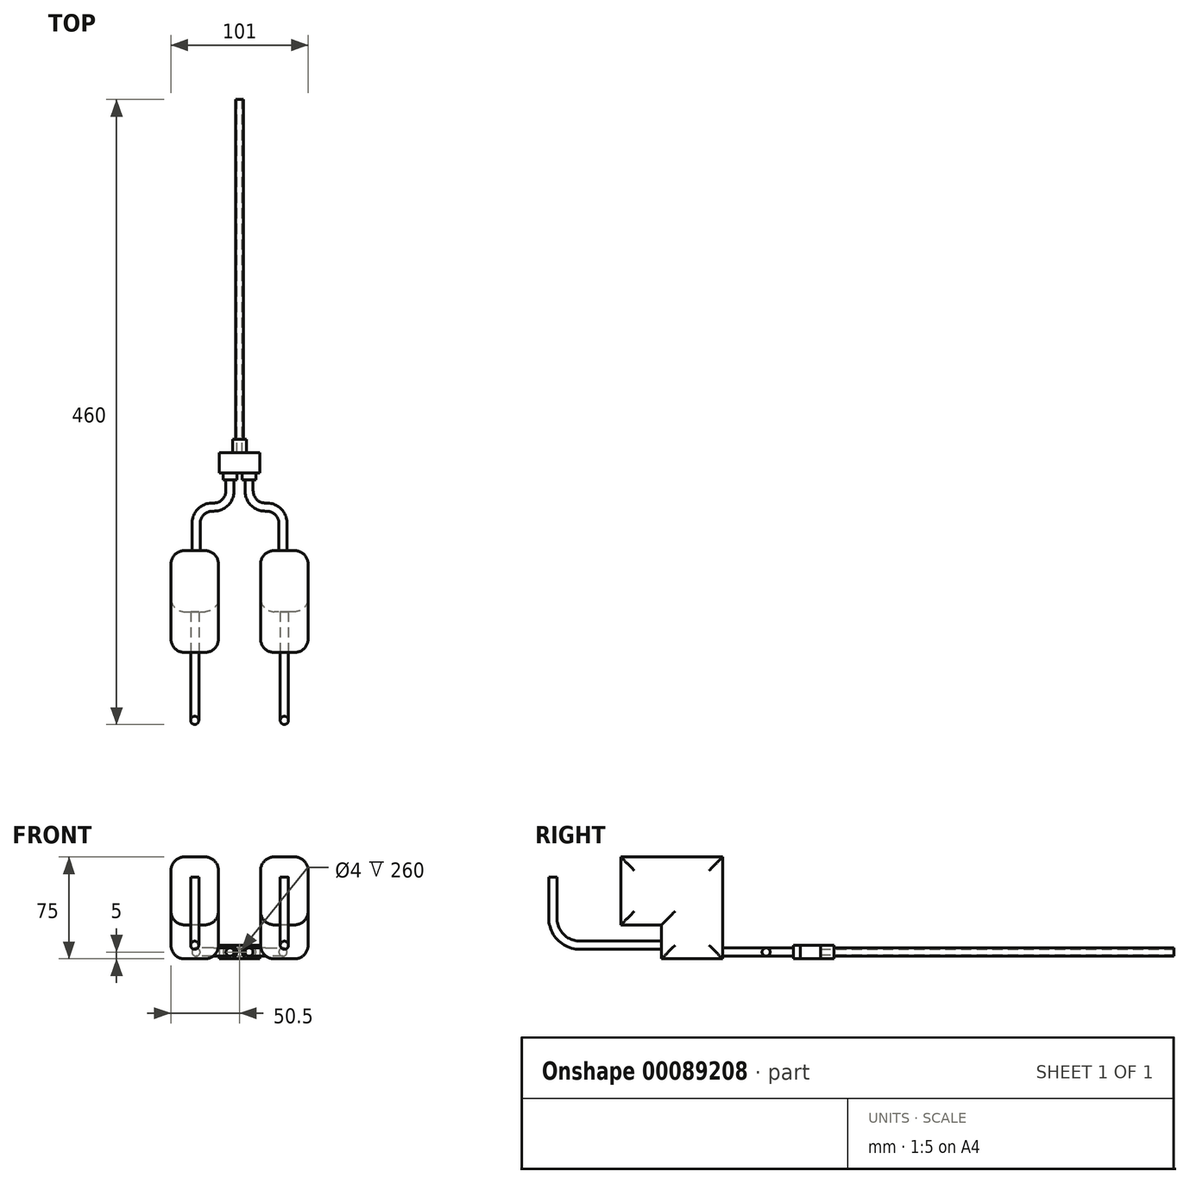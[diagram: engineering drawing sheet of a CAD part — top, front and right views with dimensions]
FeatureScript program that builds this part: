
annotation { "Feature Type Name" : "Feature", "Feature Type Description" : "" }
export const myFeature = defineFeature(function(context is Context, id is Id, definition is map)
    precondition{}
    {
        {
            var Q0;
            Q0=qCreatedBy(makeId("Front.planeOp"),FACE);
            var sketch = newSketch(context, id + "F0", { "sketchPlane" : qUnion([Q0])});
            skCircle(sketch, "E0", {"center": v(0, 0) * mm, "radius": 3 * mm});
            skCircle(sketch, "E1", {"center": v(0, 0) * mm, "radius": 2 * mm});
            skSolve(sketch);
        }
        {
            var Q0;
            Q0=makeQuery(id+"F0.imprint","IMPRINT",FACE,{"disambiguationData":[TD([[makeQuery(id+"F0.imprint","IMPRINT",EDGE,{"derivedFrom":sQuery(id+"F0.wireOp",EDGE,"E0")}),1.0]])]});
            extrude(context, id + "F1", {"entities" : qUnion([Q0]), "depth" : 250 * mm});
        }
        {
            var Q0;
            Q0=makeQuery(id+"F1.opExtrude","CAP_FACE",FACE,{"disambiguationData":[OSD([sQuery(id+"F0.wireOp",EDGE,"E0"),sQuery(id+"F0.wireOp",EDGE,"E1")])],"isStart":false});
            var sketch = newSketch(context, id + "F2", { "sketchPlane" : qUnion([Q0])});
            skCircle(sketch, "E2", {"center": v(0, 0) * mm, "radius": 5 * mm});
            skSolve(sketch);
        }
        {
            var Q0;
            Q0=makeQuery(id+"F2.imprint","IMPRINT",FACE,{"disambiguationData":[TD([[makeQuery(id+"F2.imprint","IMPRINT",EDGE,{"derivedFrom":sQuery(id+"F2.wireOp",EDGE,"E2")}),1.0]])]});
            var Q1;
            Q1=makeQuery(id+"F2.imprint","IMPRINT",FACE,{"disambiguationData":[TD([[makeQuery(id+"F2.imprint","IMPRINT",EDGE,{"derivedFrom":makeQuery(id+"F1.opExtrude","CAP_EDGE",EDGE,{"disambiguationData":[OSD([sQuery(id+"F0.wireOp",EDGE,"E0")])],"isStart":false})}),1.0]])]});
            extrude(context, id + "F3", {"entities" : qUnion([Q0, Q1]), "operationType" : NewBodyOperationType.ADD, "depth" : 10 * mm});
        }
        {
            var Q0;
            Q0=makeQuery(id+"F3.opExtrude","CAP_FACE",FACE,{"disambiguationData":[OSD([sQuery(id+"F0.wireOp",EDGE,"E1"),sQuery(id+"F2.wireOp",EDGE,"E2")])],"isStart":false});
            var sketch = newSketch(context, id + "F4", { "sketchPlane" : qUnion([Q0])});
            skLineSegment(sketch, "E3.bottom", {"start": v(15, 5) * mm, "end": v(-15, 5) * mm});
            skLineSegment(sketch, "E3.top", {"start": v(15, -5) * mm, "end": v(-15, -5) * mm});
            skLineSegment(sketch, "E3.left", {"start": v(15, 5) * mm, "end": v(15, -5) * mm});
            skLineSegment(sketch, "E3.right", {"start": v(-15, 5) * mm, "end": v(-15, -5) * mm});
            skSolve(sketch);
        }
        {
            var Q0;
            {var subQ0=sQuery(id+"F4.wireOp",EDGE,"E3.right");Q0=makeQuery(id+"F4.imprint","IMPRINT",FACE,{"disambiguationData":[TD([[makeQuery(id+"F4.imprint","IMPRINT",EDGE,{"derivedFrom":subQ0}),1.0]])]});}
            var Q1;
            Q1=makeQuery(id+"F4.imprint","IMPRINT",FACE,{"disambiguationData":[TD([[makeQuery(id+"F4.imprint","IMPRINT",EDGE,{"derivedFrom":makeQuery(id+"F3.opExtrude","CAP_EDGE",EDGE,{"disambiguationData":[OSD([sQuery(id+"F0.wireOp",EDGE,"E1")])],"isStart":false})}),-1.0]])]});
            var Q2;
            {var subQ0=sQuery(id+"F4.wireOp",EDGE,"E3.left");Q2=makeQuery(id+"F4.imprint","IMPRINT",FACE,{"disambiguationData":[TD([[makeQuery(id+"F4.imprint","IMPRINT",EDGE,{"derivedFrom":subQ0}),-1.0]])]});}
            var Q3;
            Q3=makeQuery(id+"F4.imprint","IMPRINT",FACE,{"disambiguationData":[TD([[makeQuery(id+"F4.imprint","IMPRINT",EDGE,{"derivedFrom":makeQuery(id+"F3.opExtrude","CAP_EDGE",EDGE,{"disambiguationData":[OSD([sQuery(id+"F0.wireOp",EDGE,"E1")])],"isStart":false})}),1.0]])]});
            extrude(context, id + "F5", {"entities" : qUnion([Q0, Q1, Q2, Q3]), "operationType" : NewBodyOperationType.ADD, "depth" : 15 * mm});
        }
        {
            var Q0;
            Q0=makeQuery(id+"F5.opExtrude","CAP_FACE",FACE,{"disambiguationData":[OSD([sQuery(id+"F4.wireOp",EDGE,"E3.bottom"),sQuery(id+"F4.wireOp",EDGE,"E3.top"),sQuery(id+"F4.wireOp",EDGE,"E3.left"),sQuery(id+"F4.wireOp",EDGE,"E3.right")])],"isStart":false});
            var sketch = newSketch(context, id + "F6", { "sketchPlane" : qUnion([Q0])});
            skCircle(sketch, "E4", {"center": v(-7, 0) * mm, "radius": 5 * mm});
            skCircle(sketch, "E5", {"center": v(7, 0) * mm, "radius": 5 * mm});
            skCircle(sketch, "E6", {"center": v(7, 0) * mm, "radius": 3 * mm});
            skCircle(sketch, "E7", {"center": v(-7, 0) * mm, "radius": 3 * mm});
            skSolve(sketch);
        }
        {
            var Q0;
            Q0=makeQuery(id+"F6.imprint","IMPRINT",FACE,{"disambiguationData":[TD([[makeQuery(id+"F6.imprint","IMPRINT",EDGE,{"derivedFrom":sQuery(id+"F6.wireOp",EDGE,"E7")}),-1.0]])]});
            var Q1;
            Q1=makeQuery(id+"F6.imprint","IMPRINT",FACE,{"disambiguationData":[TD([[makeQuery(id+"F6.imprint","IMPRINT",EDGE,{"derivedFrom":sQuery(id+"F6.wireOp",EDGE,"E6")}),-1.0]])]});
            extrude(context, id + "F7", {"entities" : qUnion([Q0, Q1]), "operationType" : NewBodyOperationType.ADD, "depth" : 5 * mm});
        }
        {
            var Q0;
            Q0=makeQuery(id+"F7.boolean.opBoolean","SPLIT",FACE,{"disambiguationData":[TD([makeQuery(id+"F7.opExtrude","SWEPT_FACE",FACE,{"disambiguationData":[OSD([sQuery(id+"F6.wireOp",EDGE,"E7")])]})])],"derivedFrom":makeQuery(id+"F5.opExtrude","CAP_FACE",FACE,{"disambiguationData":[OSD([sQuery(id+"F4.wireOp",EDGE,"E3.bottom"),sQuery(id+"F4.wireOp",EDGE,"E3.top"),sQuery(id+"F4.wireOp",EDGE,"E3.left"),sQuery(id+"F4.wireOp",EDGE,"E3.right")])],"isStart":false})});
            var sketch = newSketch(context, id + "F8", { "sketchPlane" : qUnion([Q0])});
            skCircle(sketch, "E8", {"center": v(-7, 0) * mm, "radius": 3 * mm});
            skCircle(sketch, "E9", {"center": v(7, 0) * mm, "radius": 3 * mm});
            skSolve(sketch);
        }
        {
            var Q0;
            Q0=qCreatedBy(makeId("Top.planeOp"),FACE);
            var sketch = newSketch(context, id + "F9", { "sketchPlane" : qUnion([Q0])});
            skLineSegment(sketch, "E10", {"start": v(-7, -275) * mm, "end": v(-7, -288) * mm});
            skLineSegment(sketch, "E11", {"start": v(-19, -300) * mm, "end": v(-20, -300) * mm});
            skLineSegment(sketch, "E12", {"start": v(7, -275) * mm, "end": v(7, -288) * mm});
            skLineSegment(sketch, "E13", {"start": v(19, -300) * mm, "end": v(20, -300) * mm});
            skLineSegment(sketch, "E14", {"start": v(-32, -312) * mm, "end": v(-32, -332) * mm});
            skLineSegment(sketch, "E15", {"start": v(32, -312) * mm, "end": v(32, -332) * mm});
            skPoint(sketch, "E16.visualSharp", {"position": v(-32, -300) * mm});
            skArc(sketch, "E16.filletArc", {"start": v(-20, -300) * mm, "mid": v(-28.49, -303.51) * mm, "end": v(-32, -312) * mm});
            skPoint(sketch, "E17.visualSharp", {"position": v(-7, -300) * mm});
            skArc(sketch, "E17.filletArc", {"start": v(-19, -300) * mm, "mid": v(-10.51, -296.49) * mm, "end": v(-7, -288) * mm});
            skPoint(sketch, "E18.visualSharp", {"position": v(32, -300) * mm});
            skArc(sketch, "E18.filletArc", {"start": v(32, -312) * mm, "mid": v(28.49, -303.51) * mm, "end": v(20, -300) * mm});
            skPoint(sketch, "E19.visualSharp", {"position": v(7, -300) * mm});
            skArc(sketch, "E19.filletArc", {"start": v(7, -288) * mm, "mid": v(10.51, -296.49) * mm, "end": v(19, -300) * mm});
            skSolve(sketch);
        }
        {
            var Q0;
            Q0=makeQuery(id+"F8.imprint","IMPRINT",FACE,{"disambiguationData":[TD([[makeQuery(id+"F8.imprint","IMPRINT",EDGE,{"derivedFrom":sQuery(id+"F8.wireOp",EDGE,"E8")}),1.0]])]});
            var Q1;
            Q1=sQuery(id+"F9.wireOp",EDGE,"E10");
            var Q2;
            Q2=sQuery(id+"F9.wireOp",EDGE,"E17.filletArc");
            var Q3;
            Q3=sQuery(id+"F9.wireOp",EDGE,"E11");
            var Q4;
            Q4=sQuery(id+"F9.wireOp",EDGE,"E16.filletArc");
            var Q5;
            Q5=sQuery(id+"F9.wireOp",EDGE,"E14");
            sweep(context, id + "F10", {"operationType" : NewBodyOperationType.ADD, "profiles" : qUnion([Q0]), "path" : qUnion([Q1, Q2, Q3, Q4, Q5])});
        }
        {
            var Q0;
            Q0=makeQuery(id+"F1.opExtrude","SWEPT_BODY",BODY,{"disambiguationData":[OSD([sQuery(id+"F0.wireOp",EDGE,"E0"),sQuery(id+"F0.wireOp",EDGE,"E1")])]});
            var Q1;
            Q1=qCreatedBy(makeId("Right.planeOp"),FACE);
            mirror(context, id + "F11", {"operationType" : NewBodyOperationType.ADD, "entities" : qUnion([Q0]), "mirrorPlane" : qUnion([Q1])});
        }
        {
            var Q0;
            Q0=makeQuery(id+"F10.opSweep","CAP_FACE",FACE,{"disambiguationData":[OSD([sQuery(id+"F8.wireOp",EDGE,"E8"),sQuery(id+"F9.wireOp",VERTEX,"E14.end")])],"isStart":false});
            var sketch = newSketch(context, id + "F12", { "sketchPlane" : qUnion([Q0])});
            skLineSegment(sketch, "E20.bottom", {"start": v(-50.5, -5) * mm, "end": v(-15.5, -5) * mm});
            skLineSegment(sketch, "E20.top", {"start": v(-50.5, 70) * mm, "end": v(-15.5, 70) * mm});
            skLineSegment(sketch, "E20.left", {"start": v(-50.5, -5) * mm, "end": v(-50.5, 70) * mm});
            skLineSegment(sketch, "E20.right", {"start": v(-15.5, -5) * mm, "end": v(-15.5, 70) * mm});
            skLineSegment(sketch, "E21.bottom", {"start": v(15.5, -5) * mm, "end": v(50.5, -5) * mm});
            skLineSegment(sketch, "E21.top", {"start": v(15.5, 70) * mm, "end": v(50.5, 70) * mm});
            skLineSegment(sketch, "E21.left", {"start": v(15.5, -5) * mm, "end": v(15.5, 70) * mm});
            skLineSegment(sketch, "E21.right", {"start": v(50.5, -5) * mm, "end": v(50.5, 70) * mm});
            skSolve(sketch);
        }
        {
            var Q0;
            Q0=makeQuery(id+"F12.imprint","IMPRINT",FACE,{"disambiguationData":[TD([[makeQuery(id+"F12.imprint","IMPRINT",EDGE,{"derivedFrom":sQuery(id+"F12.wireOp",EDGE,"E20.bottom")}),1.0]])]});
            var Q1;
            Q1=makeQuery(id+"F12.imprint","IMPRINT",FACE,{"disambiguationData":[TD([[makeQuery(id+"F12.imprint","IMPRINT",EDGE,{"derivedFrom":sQuery(id+"F12.wireOp",EDGE,"E21.bottom")}),1.0]])]});
            var Q2;
            Q2=makeQuery(id+"F12.imprint","IMPRINT",FACE,{"disambiguationData":[TD([[makeQuery(id+"F12.imprint","IMPRINT",EDGE,{"derivedFrom":makeQuery(id+"F10.opSweep","CAP_EDGE",EDGE,{"disambiguationData":[OSD([sQuery(id+"F8.wireOp",EDGE,"E8"),sQuery(id+"F9.wireOp",VERTEX,"E14.end")])],"isStart":false})}),1.0]])]});
            extrude(context, id + "F13", {"entities" : qUnion([Q0, Q1, Q2]), "operationType" : NewBodyOperationType.ADD, "depth" : 75 * mm});
        }
        {
            var Q0;
            Q0=makeQuery(id+"F13.opExtrude","CAP_FACE",FACE,{"disambiguationData":[OSD([sQuery(id+"F12.wireOp",EDGE,"E20.bottom"),sQuery(id+"F12.wireOp",EDGE,"E20.top"),sQuery(id+"F12.wireOp",EDGE,"E20.left"),sQuery(id+"F12.wireOp",EDGE,"E20.right")])],"isStart":false});
            var sketch = newSketch(context, id + "F14", { "sketchPlane" : qUnion([Q0])});
            skLineSegment(sketch, "E22.bottom", {"start": v(-15.5, -5) * mm, "end": v(-50.5, -5) * mm});
            skLineSegment(sketch, "E22.top", {"start": v(-15.5, 20) * mm, "end": v(-50.5, 20) * mm});
            skLineSegment(sketch, "E22.left", {"start": v(-15.5, -5) * mm, "end": v(-15.5, 20) * mm});
            skLineSegment(sketch, "E22.right", {"start": v(-50.5, -5) * mm, "end": v(-50.5, 20) * mm});
            skLineSegment(sketch, "E23.bottom", {"start": v(50.5, -5) * mm, "end": v(15.5, -5) * mm});
            skLineSegment(sketch, "E23.top", {"start": v(50.5, 20) * mm, "end": v(15.5, 20) * mm});
            skLineSegment(sketch, "E23.left", {"start": v(50.5, -5) * mm, "end": v(50.5, 20) * mm});
            skLineSegment(sketch, "E23.right", {"start": v(15.5, -5) * mm, "end": v(15.5, 20) * mm});
            skSolve(sketch);
        }
        {
            var Q0;
            Q0=makeQuery(id+"F14.imprint","IMPRINT",FACE,{"disambiguationData":[TD([[makeQuery(id+"F14.imprint","IMPRINT",EDGE,{"derivedFrom":sQuery(id+"F14.wireOp",EDGE,"E22.bottom")}),1.0]])]});
            var Q1;
            Q1=makeQuery(id+"F14.imprint","IMPRINT",FACE,{"disambiguationData":[TD([[makeQuery(id+"F14.imprint","IMPRINT",EDGE,{"derivedFrom":sQuery(id+"F14.wireOp",EDGE,"E23.bottom")}),-1.0]])]});
            extrude(context, id + "F15", {"entities" : qUnion([Q0, Q1]), "operationType" : NewBodyOperationType.REMOVE, "oppositeDirection" : true, "depth" : 30 * mm});
        }
        {
            var Q0;
            Q0=makeQuery(id+"F13.opExtrude","SWEPT_FACE",FACE,{"disambiguationData":[OSD([sQuery(id+"F12.wireOp",EDGE,"E20.left")])]});
            var Q1;
            Q1=makeQuery(id+"F13.opExtrude","SWEPT_FACE",FACE,{"disambiguationData":[OSD([sQuery(id+"F12.wireOp",EDGE,"E20.right")])]});
            var Q2;
            Q2=makeQuery(id+"F13.opExtrude","SWEPT_FACE",FACE,{"disambiguationData":[OSD([sQuery(id+"F12.wireOp",EDGE,"E21.right")])]});
            var Q3;
            Q3=makeQuery(id+"F13.opExtrude","SWEPT_FACE",FACE,{"disambiguationData":[OSD([sQuery(id+"F12.wireOp",EDGE,"E21.left")])]});
            fillet(context, id + "F16", {"entities" : qUnion([Q0, Q1, Q2, Q3]), "radius" : 10 * mm, "tangentPropagation" : true, "allowEdgeOverflow" : false});
        }
        {
            var Q0;
            Q0=makeQuery(id+"F13.opExtrude","SWEPT_FACE",FACE,{"disambiguationData":[OSD([sQuery(id+"F12.wireOp",EDGE,"E20.left")])]});
            cPlane(context, id + "F17", {"entities" : qUnion([Q0]), "cplaneType" : CPlaneType.OFFSET, "offset" : 17.5 * mm, "oppositeDirection" : true, "width" : 150 * mm, "height" : 150 * mm});
        }
        {
            var Q0;
            Q0=makeQuery(id+"F15.boolean.opBoolean","COPY",FACE,{"derivedFrom":makeQuery(id+"F15.opExtrude","CAP_FACE",FACE,{"disambiguationData":[OSD([sQuery(id+"F14.wireOp",EDGE,"E22.bottom"),sQuery(id+"F14.wireOp",EDGE,"E22.top"),sQuery(id+"F14.wireOp",EDGE,"E22.left"),sQuery(id+"F14.wireOp",EDGE,"E22.right")])],"isStart":false})});
            var sketch = newSketch(context, id + "F18", { "sketchPlane" : qUnion([Q0])});
            skCircle(sketch, "E24", {"center": v(-33, 5) * mm, "radius": 3 * mm});
            skSolve(sketch);
        }
        {
            var Q0;
            Q0=qCreatedBy(id+"F17.planeOp",FACE);
            var sketch = newSketch(context, id + "F19", { "sketchPlane" : qUnion([Q0])});
            skLineSegment(sketch, "E25", {"start": v(377, 5) * mm, "end": v(437, 5) * mm});
            skLineSegment(sketch, "E26", {"start": v(457, 25) * mm, "end": v(457, 55) * mm});
            skPoint(sketch, "E27.visualSharp", {"position": v(457, 5) * mm});
            skArc(sketch, "E27.filletArc", {"start": v(437, 5) * mm, "mid": v(451.14, 10.86) * mm, "end": v(457, 25) * mm});
            skSolve(sketch);
        }
        {
            var Q0;
            Q0=makeQuery(id+"F18.imprint","IMPRINT",FACE,{"disambiguationData":[TD([[makeQuery(id+"F18.imprint","IMPRINT",EDGE,{"derivedFrom":sQuery(id+"F18.wireOp",EDGE,"E24")}),1.0]])]});
            var Q1;
            Q1=sQuery(id+"F19.wireOp",EDGE,"E25");
            var Q2;
            Q2=sQuery(id+"F19.wireOp",EDGE,"E27.filletArc");
            var Q3;
            Q3=sQuery(id+"F19.wireOp",EDGE,"E26");
            sweep(context, id + "F20", {"operationType" : NewBodyOperationType.ADD, "profiles" : qUnion([Q0]), "path" : qUnion([Q1, Q2, Q3])});
        }
        {
            var Q0;
            Q0=makeQuery(id+"F1.opExtrude","SWEPT_BODY",BODY,{"disambiguationData":[OSD([sQuery(id+"F0.wireOp",EDGE,"E0"),sQuery(id+"F0.wireOp",EDGE,"E1")])]});
            var Q1;
            Q1=qCreatedBy(makeId("Right.planeOp"),FACE);
            mirror(context, id + "F21", {"operationType" : NewBodyOperationType.ADD, "entities" : qUnion([Q0]), "mirrorPlane" : qUnion([Q1])});
        }
    });
